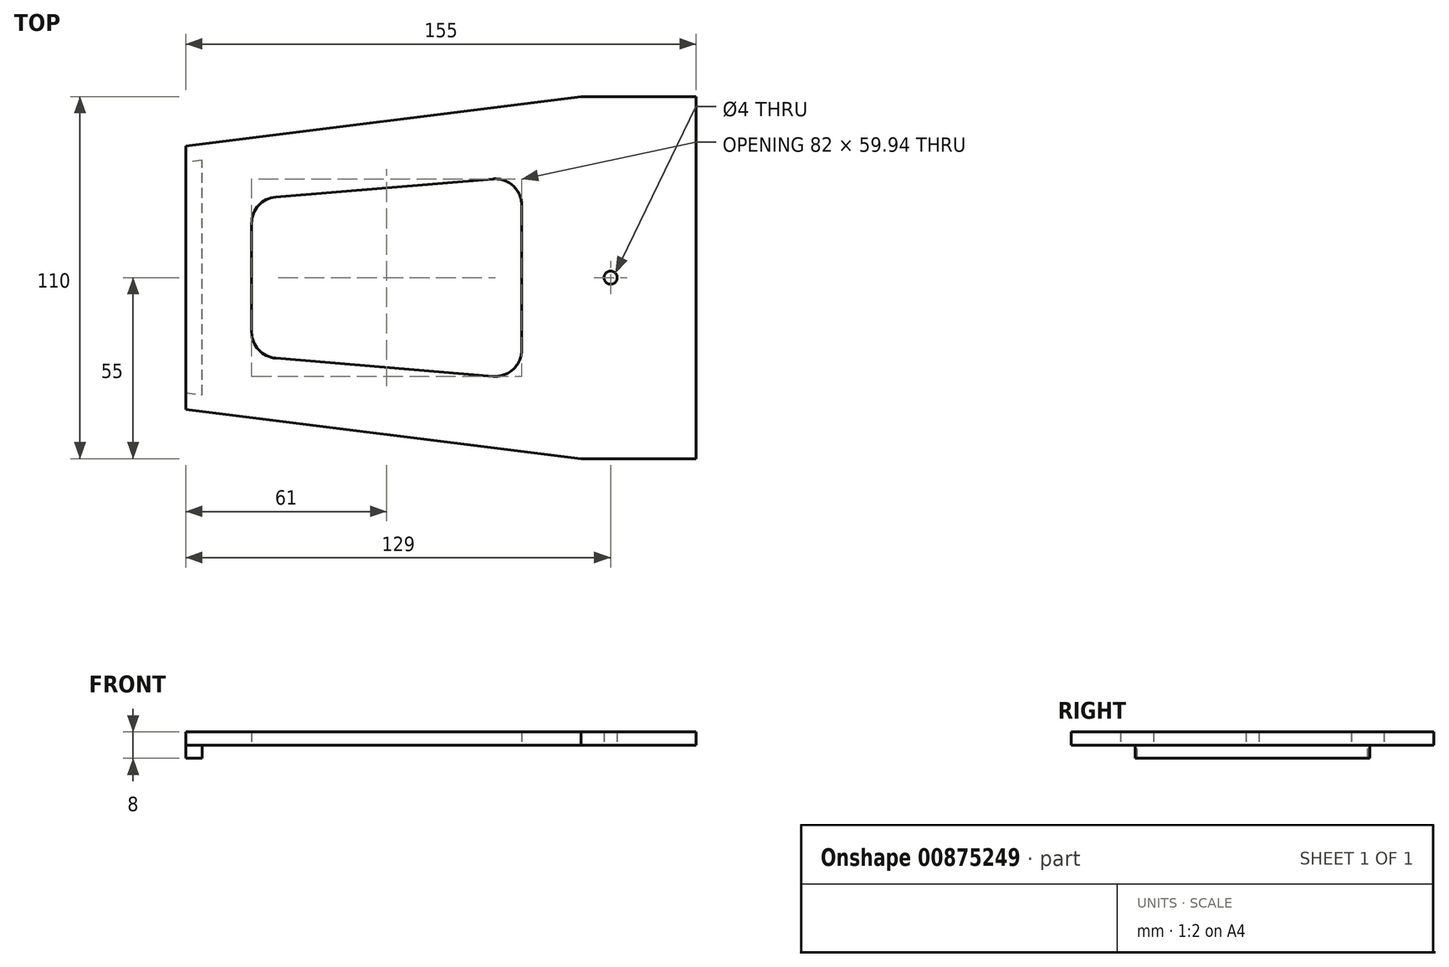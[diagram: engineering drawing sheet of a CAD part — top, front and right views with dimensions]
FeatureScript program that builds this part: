
annotation { "Feature Type Name" : "Feature", "Feature Type Description" : "" }
export const myFeature = defineFeature(function(context is Context, id is Id, definition is map)
    precondition{}
    {
        {
            var Q0;
            Q0=qCreatedBy(makeId("Top.planeOp"),FACE);
            var sketch = newSketch(context, id + "F0", { "sketchPlane" : qUnion([Q0])});
            skLineSegment(sketch, "E0", {"start": v(0, 40) * mm, "end": v(0, -40) * mm});
            skLineSegment(sketch, "E1", {"start": v(0, -40) * mm, "end": v(120, -55) * mm});
            skLineSegment(sketch, "E2", {"start": v(120, -55) * mm, "end": v(155, -55) * mm});
            skLineSegment(sketch, "E3", {"start": v(155, -55) * mm, "end": v(155, 55) * mm});
            skLineSegment(sketch, "E4", {"start": v(155, 55) * mm, "end": v(120, 55) * mm});
            skLineSegment(sketch, "E5", {"start": v(120, 55) * mm, "end": v(0, 40) * mm});
            skLineSegment(sketch, "E6", {"start": v(0, 0) * mm, "end": v(155, 0) * mm, "construction": true});
            skLineSegment(sketch, "E7", {"start": v(20, 16.5) * mm, "end": v(20, -16.5) * mm});
            skLineSegment(sketch, "E8", {"start": v(27.34, -24.47) * mm, "end": v(93.34, -29.97) * mm});
            skLineSegment(sketch, "E9", {"start": v(102, -22) * mm, "end": v(102, 22) * mm});
            skLineSegment(sketch, "E10", {"start": v(93.34, 29.97) * mm, "end": v(27.34, 24.47) * mm});
            skPoint(sketch, "E11.visualSharp", {"position": v(20, 23.86) * mm});
            skArc(sketch, "E11.filletArc", {"start": v(27.34, 24.47) * mm, "mid": v(22.11, 21.92) * mm, "end": v(20, 16.5) * mm});
            skPoint(sketch, "E12.visualSharp", {"position": v(102, 30.7) * mm});
            skArc(sketch, "E12.filletArc", {"start": v(102, 22) * mm, "mid": v(99.42, 27.89) * mm, "end": v(93.34, 29.97) * mm});
            skPoint(sketch, "E13.visualSharp", {"position": v(102, -30.7) * mm});
            skArc(sketch, "E13.filletArc", {"start": v(93.34, -29.97) * mm, "mid": v(99.42, -27.89) * mm, "end": v(102, -22) * mm});
            skPoint(sketch, "E14.visualSharp", {"position": v(20, -23.86) * mm});
            skArc(sketch, "E14.filletArc", {"start": v(20, -16.5) * mm, "mid": v(22.11, -21.92) * mm, "end": v(27.34, -24.47) * mm});
            skLineSegment(sketch, "E15", {"start": v(102, 0) * mm, "end": v(20, 0) * mm, "construction": true});
            skCircle(sketch, "E16", {"center": v(129, 0) * mm, "radius": 2 * mm});
            skSolve(sketch);
        }
        {
            var Q0;
            Q0 = qSketchRegion(id + "F0", true);
            extrude(context, id + "F1", {"entities" : qUnion([Q0]), "depth" : 4 * mm, "offsetDistance" : 25 * mm});
        }
        {
            var Q0;
            Q0=makeQuery(id+"F0.imprint","IMPRINT",FACE,{"disambiguationData":[TD([[makeQuery(id+"F0.imprint","IMPRINT",EDGE,{"derivedFrom":sQuery(id+"F0.wireOp",EDGE,"E0")}),1.0]])]});
            var sketch = newSketch(context, id + "F2", { "sketchPlane" : qUnion([Q0])});
            skLineSegment(sketch, "E17", {"start": v(0, -34.96) * mm, "end": v(5, -35.59) * mm});
            skLineSegment(sketch, "E18", {"start": v(5, -35.59) * mm, "end": v(5, 35.59) * mm});
            skLineSegment(sketch, "E19", {"start": v(5, 35.59) * mm, "end": v(0, 34.96) * mm});
            skLineSegment(sketch, "E20", {"start": v(0, 34.96) * mm, "end": v(0, -34.96) * mm});
            skSolve(sketch);
        }
        {
            var Q0;
            Q0 = qSketchRegion(id + "F2", true);
            extrude(context, id + "F3", {"entities" : qUnion([Q0]), "operationType" : NewBodyOperationType.ADD, "oppositeDirection" : true, "depth" : 4 * mm, "offsetDistance" : 25 * mm});
        }
    });
